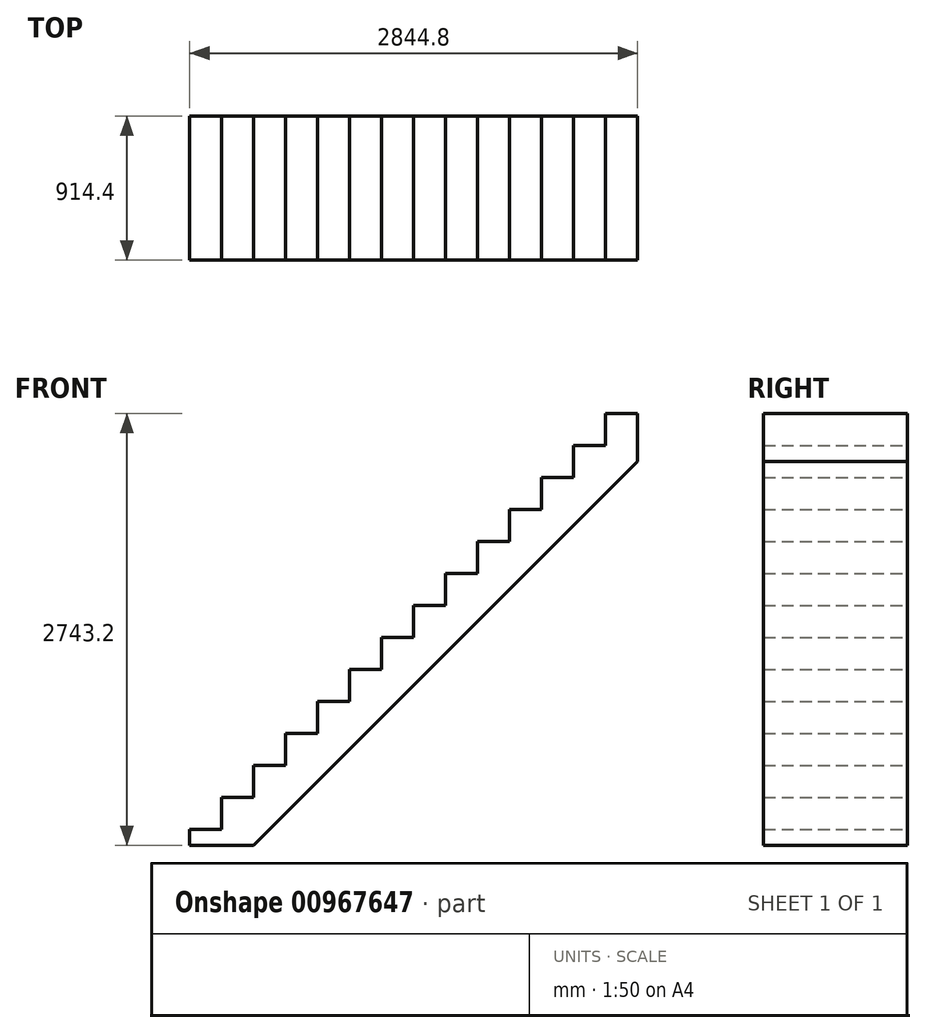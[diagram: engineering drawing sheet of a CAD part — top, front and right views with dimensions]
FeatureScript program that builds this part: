
annotation { "Feature Type Name" : "Feature", "Feature Type Description" : "" }
export const myFeature = defineFeature(function(context is Context, id is Id, definition is map)
    precondition{}
    {
        {
            var Q0;
            Q0=qCreatedBy(makeId("Front.planeOp"),FACE);
            var sketch = newSketch(context, id + "F0", { "sketchPlane" : qUnion([Q0])});
            skLineSegment(sketch, "E0", {"start": v(0, 0) * mm, "end": v(203.2, 0) * mm});
            skLineSegment(sketch, "E1", {"start": v(203.2, 0) * mm, "end": v(203.2, -304.8) * mm});
            skLineSegment(sketch, "E2", {"start": v(203.2, -304.8) * mm, "end": v(-2235.2, -2743.2) * mm});
            skLineSegment(sketch, "E3", {"start": v(0, 0) * mm, "end": v(0, -203.2) * mm});
            skLineSegment(sketch, "E4", {"start": v(0, -203.2) * mm, "end": v(-203.2, -203.2) * mm});
            skLineSegment(sketch, "E5", {"start": v(-203.2, -203.2) * mm, "end": v(-203.2, -406.4) * mm});
            skLineSegment(sketch, "E6", {"start": v(-203.2, -406.4) * mm, "end": v(-406.4, -406.4) * mm});
            skLineSegment(sketch, "E7", {"start": v(-406.4, -406.4) * mm, "end": v(-406.4, -609.6) * mm});
            skLineSegment(sketch, "E8", {"start": v(-406.4, -609.6) * mm, "end": v(-609.6, -609.6) * mm});
            skLineSegment(sketch, "E9", {"start": v(-609.6, -609.6) * mm, "end": v(-609.6, -812.8) * mm});
            skLineSegment(sketch, "E10", {"start": v(-609.6, -812.8) * mm, "end": v(-812.8, -812.8) * mm});
            skLineSegment(sketch, "E11", {"start": v(-812.8, -812.8) * mm, "end": v(-812.8, -1016) * mm});
            skLineSegment(sketch, "E12", {"start": v(-812.8, -1016) * mm, "end": v(-1016, -1016) * mm});
            skLineSegment(sketch, "E13", {"start": v(-1016, -1016) * mm, "end": v(-1016, -1219.2) * mm});
            skLineSegment(sketch, "E14", {"start": v(-1016, -1219.2) * mm, "end": v(-1219.2, -1219.2) * mm});
            skLineSegment(sketch, "E15", {"start": v(-1219.2, -1219.2) * mm, "end": v(-1219.2, -1422.4) * mm});
            skLineSegment(sketch, "E16", {"start": v(-1219.2, -1422.4) * mm, "end": v(-1422.4, -1422.4) * mm});
            skLineSegment(sketch, "E17", {"start": v(-1422.4, -1422.4) * mm, "end": v(-1422.4, -1625.6) * mm});
            skLineSegment(sketch, "E18", {"start": v(-1422.4, -1625.6) * mm, "end": v(-1625.6, -1625.6) * mm});
            skLineSegment(sketch, "E19", {"start": v(-1625.6, -1625.6) * mm, "end": v(-1625.6, -1828.8) * mm});
            skLineSegment(sketch, "E20", {"start": v(-1625.6, -1828.8) * mm, "end": v(-1828.8, -1828.8) * mm});
            skLineSegment(sketch, "E21", {"start": v(-1828.8, -1828.8) * mm, "end": v(-1828.8, -2032) * mm});
            skLineSegment(sketch, "E22", {"start": v(-1828.8, -2032) * mm, "end": v(-2032, -2032) * mm});
            skLineSegment(sketch, "E23", {"start": v(-2032, -2032) * mm, "end": v(-2032, -2235.2) * mm});
            skLineSegment(sketch, "E24", {"start": v(-2032, -2235.2) * mm, "end": v(-2235.2, -2235.2) * mm});
            skLineSegment(sketch, "E25", {"start": v(-2235.2, -2235.2) * mm, "end": v(-2235.2, -2438.4) * mm});
            skLineSegment(sketch, "E26", {"start": v(-2235.2, -2438.4) * mm, "end": v(-2438.4, -2438.4) * mm});
            skLineSegment(sketch, "E27", {"start": v(-2438.4, -2438.4) * mm, "end": v(-2438.4, -2641.6) * mm});
            skLineSegment(sketch, "E28", {"start": v(-2438.4, -2641.6) * mm, "end": v(-2641.6, -2641.6) * mm});
            skLineSegment(sketch, "E29", {"start": v(-2641.6, -2641.6) * mm, "end": v(-2641.6, -2743.2) * mm});
            skLineSegment(sketch, "E30", {"start": v(-2235.2, -2743.2) * mm, "end": v(-2641.6, -2743.2) * mm});
            skSolve(sketch);
        }
        {
            var Q0;
            Q0 = qSketchRegion(id + "F0", true);
            extrude(context, id + "F1", {"entities" : qUnion([Q0]), "depth" : 914.4 * mm, "offsetDistance" : 30.48 * mm});
        }
    });
